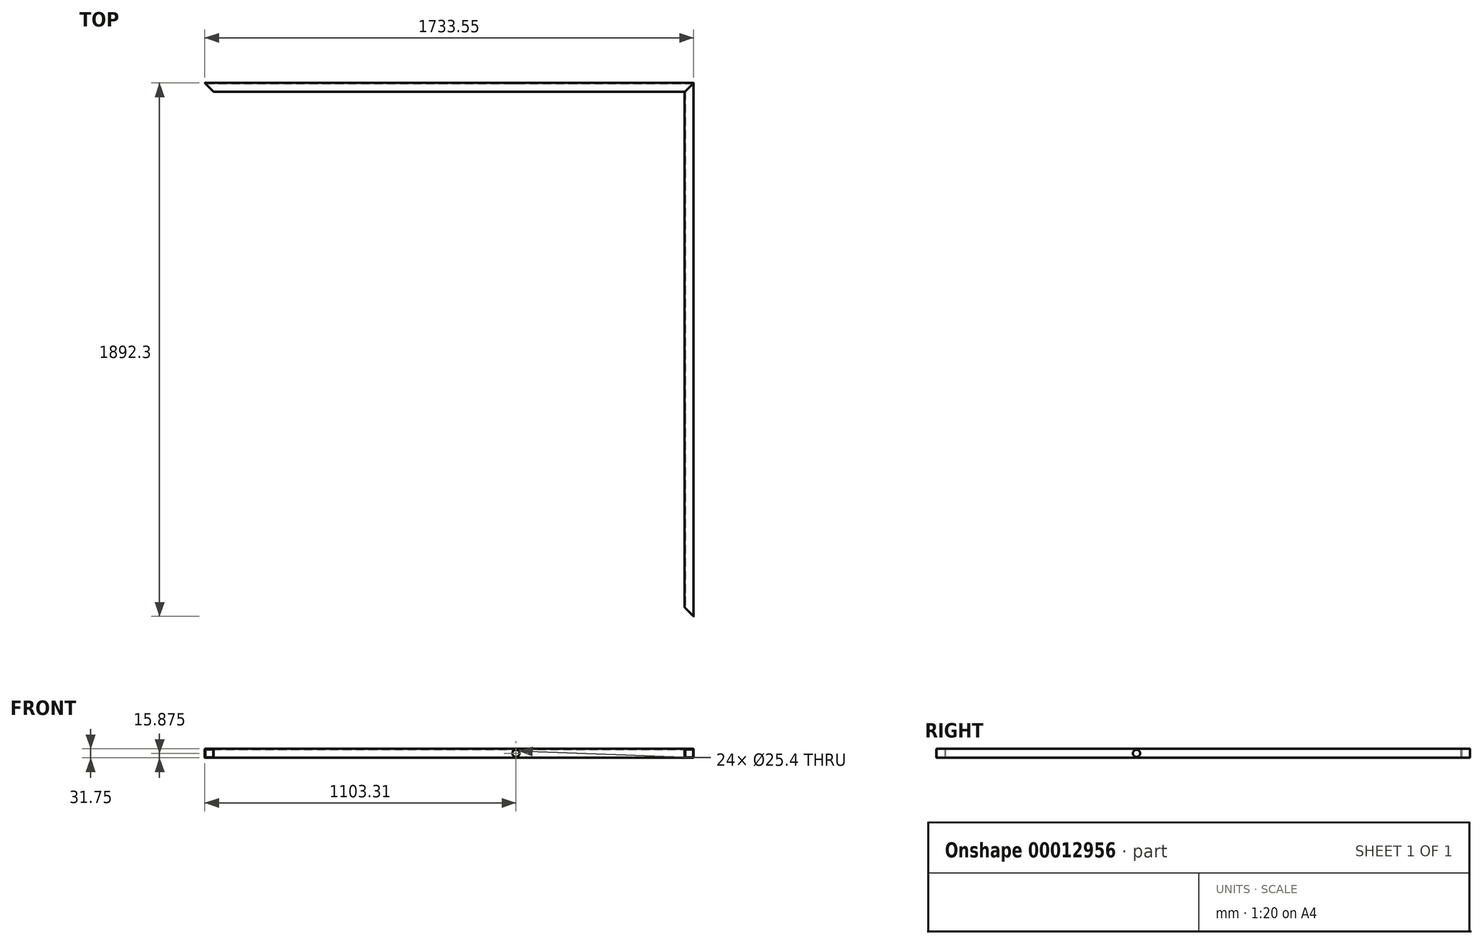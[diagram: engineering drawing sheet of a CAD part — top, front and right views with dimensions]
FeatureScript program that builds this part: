
annotation { "Feature Type Name" : "Feature", "Feature Type Description" : "" }
export const myFeature = defineFeature(function(context is Context, id is Id, definition is map)
    precondition{}
    {
        {
            var Q0;
            Q0=qCreatedBy(makeId("Top.planeOp"),FACE);
            var sketch = newSketch(context, id + "F0", { "sketchPlane" : qUnion([Q0])});
            skLineSegment(sketch, "E0.rect.bottom", {"start": v(835.02, -914.4) * mm, "end": v(-835.02, -914.4) * mm});
            skLineSegment(sketch, "E0.rect.top", {"start": v(835.03, 914.4) * mm, "end": v(-835.02, 914.4) * mm});
            skLineSegment(sketch, "E0.rect.left", {"start": v(835.02, -914.4) * mm, "end": v(835.03, 914.4) * mm});
            skLineSegment(sketch, "E0.rect.right", {"start": v(-835.02, -914.4) * mm, "end": v(-835.02, 914.4) * mm});
            skPoint(sketch, "E0.rect.middle", {"position": v(0, 0) * mm});
            skLineSegment(sketch, "E1.0", {"start": v(-866.78, -946.15) * mm, "end": v(-866.77, 946.15) * mm});
            skLineSegment(sketch, "E1.1", {"start": v(866.78, -946.15) * mm, "end": v(-866.78, -946.15) * mm});
            skLineSegment(sketch, "E1.2", {"start": v(866.78, -946.15) * mm, "end": v(866.78, 946.15) * mm});
            skLineSegment(sketch, "E1.3", {"start": v(866.78, 946.15) * mm, "end": v(-866.77, 946.15) * mm});
            skLineSegment(sketch, "E2", {"start": v(-866.77, 946.15) * mm, "end": v(-835.02, 914.4) * mm});
            skLineSegment(sketch, "E3", {"start": v(866.78, 946.15) * mm, "end": v(835.03, 914.4) * mm});
            skLineSegment(sketch, "E4", {"start": v(835.02, -914.4) * mm, "end": v(866.77, -946.15) * mm});
            skSolve(sketch);
        }
        {
            var Q0;
            Q0=makeQuery(id+"F0.imprint","IMPRINT",FACE,{"disambiguationData":[TD([[makeQuery(id+"F0.imprint","IMPRINT",EDGE,{"derivedFrom":sQuery(id+"F0.wireOp",EDGE,"E0.rect.top")}),-1.0]])]});
            extrude(context, id + "F1", {"entities" : qUnion([Q0]), "depth" : 31.75 * mm});
        }
        {
            var Q0;
            Q0=makeQuery(id+"F1.opExtrude","CAP_EDGE",EDGE,{"disambiguationData":[OSD([sQuery(id+"F0.wireOp",EDGE,"E0.rect.top")])],"isStart":false});
            var Q1;
            Q1=makeQuery(id+"F1.opExtrude","CAP_EDGE",EDGE,{"disambiguationData":[OSD([sQuery(id+"F0.wireOp",EDGE,"E1.3")])],"isStart":false});
            var Q2;
            Q2=makeQuery(id+"F1.opExtrude","CAP_EDGE",EDGE,{"disambiguationData":[OSD([sQuery(id+"F0.wireOp",EDGE,"E0.rect.top")])],"isStart":true});
            var Q3;
            Q3=makeQuery(id+"F1.opExtrude","CAP_EDGE",EDGE,{"disambiguationData":[OSD([sQuery(id+"F0.wireOp",EDGE,"E1.3")])],"isStart":true});
            fillet(context, id + "F2", {"entities" : qUnion([Q0, Q1, Q2, Q3]), "radius" : 1.6 * mm, "tangentPropagation" : true, "allowEdgeOverflow" : false});
        }
        {
            var Q0;
            Q0=makeQuery(id+"F1.opExtrude","SWEPT_FACE",FACE,{"disambiguationData":[OSD([sQuery(id+"F0.wireOp",EDGE,"E3")])]});
            var Q1;
            Q1=makeQuery(id+"F1.opExtrude","SWEPT_FACE",FACE,{"disambiguationData":[OSD([sQuery(id+"F0.wireOp",EDGE,"E2")])]});
            var Q2;
            Q2=makeQuery(id+"F1.opExtrude","SWEPT_BODY",BODY,{"disambiguationData":[OSD([sQuery(id+"F0.wireOp",EDGE,"E0.rect.top"),sQuery(id+"F0.wireOp",EDGE,"E1.3"),sQuery(id+"F0.wireOp",EDGE,"E2"),sQuery(id+"F0.wireOp",EDGE,"E3")])]});
            shell(context, id + "F3", {"entities" : qUnion([Q0, Q1]), "parts" : qUnion([Q2]), "thickness" : 2.1 * mm});
        }
        {
            var Q0;
            Q0=makeQuery(id+"F0.imprint","IMPRINT",FACE,{"disambiguationData":[TD([[makeQuery(id+"F0.imprint","IMPRINT",EDGE,{"derivedFrom":sQuery(id+"F0.wireOp",EDGE,"E0.rect.left")}),-1.0]])]});
            extrude(context, id + "F4", {"entities" : qUnion([Q0]), "depth" : 31.75 * mm});
        }
        {
            var Q0;
            Q0=makeQuery(id+"F4.opExtrude","CAP_EDGE",EDGE,{"disambiguationData":[OSD([sQuery(id+"F0.wireOp",EDGE,"E1.2")])],"isStart":false});
            var Q1;
            Q1=makeQuery(id+"F4.opExtrude","CAP_EDGE",EDGE,{"disambiguationData":[OSD([sQuery(id+"F0.wireOp",EDGE,"E1.2")])],"isStart":true});
            var Q2;
            Q2=makeQuery(id+"F4.opExtrude","CAP_EDGE",EDGE,{"disambiguationData":[OSD([sQuery(id+"F0.wireOp",EDGE,"E0.rect.left")])],"isStart":true});
            var Q3;
            Q3=makeQuery(id+"F4.opExtrude","CAP_EDGE",EDGE,{"disambiguationData":[OSD([sQuery(id+"F0.wireOp",EDGE,"E0.rect.left")])],"isStart":false});
            fillet(context, id + "F5", {"entities" : qUnion([Q0, Q1, Q2, Q3]), "radius" : 1.6 * mm, "tangentPropagation" : true, "allowEdgeOverflow" : false});
        }
        {
            var Q0;
            Q0=makeQuery(id+"F4.opExtrude","SWEPT_FACE",FACE,{"disambiguationData":[OSD([sQuery(id+"F0.wireOp",EDGE,"E3")])]});
            var Q1;
            Q1=makeQuery(id+"F4.opExtrude","SWEPT_FACE",FACE,{"disambiguationData":[OSD([sQuery(id+"F0.wireOp",EDGE,"E4")])]});
            shell(context, id + "F6", {"entities" : qUnion([Q0, Q1]), "thickness" : 2.1 * mm});
        }
        {
            var Q0;
            Q0=makeQuery(id+"F1.opExtrude","SWEPT_FACE",FACE,{"disambiguationData":[OSD([sQuery(id+"F0.wireOp",EDGE,"E0.rect.top")])]});
            var sketch = newSketch(context, id + "F7", { "sketchPlane" : qUnion([Q0])});
            skLineSegment(sketch, "E5", {"start": v(835.03, 15.88) * mm, "end": v(236.54, 15.88) * mm});
            skCircle(sketch, "E6", {"center": v(236.54, 15.88) * mm, "radius": 12.7 * mm});
            skSolve(sketch);
        }
        {
            var Q0;
            Q0=makeQuery(id+"F7.imprint","IMPRINT",FACE,{"disambiguationData":[TD([[makeQuery(id+"F7.imprint","IMPRINT",EDGE,{"derivedFrom":sQuery(id+"F7.wireOp",EDGE,"E6")}),1.0]])]});
            extrude(context, id + "F8", {"entities" : qUnion([Q0]), "operationType" : NewBodyOperationType.REMOVE, "endBound" : BoundingType.THROUGH_ALL, "oppositeDirection" : true, "depth" : 25.4 * mm});
        }
        {
            var Q0;
            Q0=makeQuery(id+"F4.opExtrude","SWEPT_FACE",FACE,{"disambiguationData":[OSD([sQuery(id+"F0.wireOp",EDGE,"E0.rect.left")])]});
            var sketch = newSketch(context, id + "F9", { "sketchPlane" : qUnion([Q0])});
            skLineSegment(sketch, "E7", {"start": v(914.4, 15.88) * mm, "end": v(236.54, 15.87) * mm});
            skCircle(sketch, "E8", {"center": v(236.54, 15.87) * mm, "radius": 12.7 * mm});
            skSolve(sketch);
        }
        {
            var Q0;
            Q0=makeQuery(id+"F9.imprint","IMPRINT",FACE,{"disambiguationData":[TD([[makeQuery(id+"F9.imprint","IMPRINT",EDGE,{"derivedFrom":sQuery(id+"F9.wireOp",EDGE,"E8")}),1.0]])]});
            extrude(context, id + "F10", {"entities" : qUnion([Q0]), "operationType" : NewBodyOperationType.REMOVE, "endBound" : BoundingType.THROUGH_ALL, "oppositeDirection" : true, "depth" : 25.4 * mm});
        }
    });
